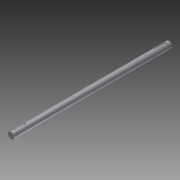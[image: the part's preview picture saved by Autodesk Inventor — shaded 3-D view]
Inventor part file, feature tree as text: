
AUTODESK INVENTOR PART (.ipt)
format: ipt  version: 2012 (Build 160160000, 160)  size: 123,392 bytes
history: native  units: in
note: dims shown in document units (in); Inventor stores cm internally (conversion verified against a paired STEP export)
features: extrude x4, sketch x4, plane x3, projected_geometry x1
ambient origin geometry x8: Origin, YZ Plane, XZ Plane, XY Plane, X Axis, Y Axis, Z Axis, Center Point
bodies: Solid1 (feature_tree)
feature tree (12):
  extrude  "Extrusion1"  Depth=12.375in TaperAngle=0.0deg
  plane  "Work Plane1"
  sketch  "Sketch2"  dims[d3=11.875in d4=0.25in]
  plane  "Work Plane2"
  plane  "Work Plane3"
  extrude  "Extrusion2"  Depth=0.25in
  extrude  "Extrusion3"  Depth=0.4in
  extrude  "Extrusion4"  Depth=0.04in TaperAngle=0.0deg
  sketch  "Sketch1"  dims[d0=0.5in d1=12.375in d2=0.0in]
  projected_geometry  "Projected Loop1"
  sketch  "Sketch3"  dims[d5=0.25in d6=0.4in]
  sketch  "Sketch4"  dims[d7=0.04in d8=0.0in d9=0.04in d10=0.0in d11=0.75in d12=0.125in d13=0.75in d14=0.125in d15=0.3125in d16=11.0in d17=0.25in d18=0.0625in d19=0.0in]
